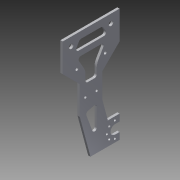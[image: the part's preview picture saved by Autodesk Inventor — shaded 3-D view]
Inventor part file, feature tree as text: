
AUTODESK INVENTOR PART (.ipt)
format: ipt  version: 2013 (Build 170138000, 138)  size: 265,728 bytes
history: native  units: mm
features: sketch x8, extrude x6, fillet x3, hole x2, other x1, pattern_circular x1
ambient origin geometry x8: Origin, YZ Plane, XZ Plane, XY Plane, X Axis, Y Axis, Z Axis, Center Point
feature tree (21):
  other  "ソリッド1"
  extrude  "押し出し1"  Depth=50.0mm
  extrude  "押し出し2"  Depth=100.0mm
  extrude  "押し出し5"  Depth=50.0mm
  hole  "穴1"  [1 undecoded]
  pattern_circular  "円形状パターン2"  [2 undecoded]
  hole  "穴2"  [1 undecoded]
  extrude  "押し出し7"  TaperAngle=135.0deg  [1 undecoded]
  extrude  "押し出し8"  Depth=25.0mm
  fillet  "フィレット1"  Radius=25.0mm
  fillet  "フィレット2"  Radius=50.0mm
  extrude  "押し出し9"  TaperAngle=165.0deg  [1 undecoded]
  fillet  "フィレット3"  Radius=20.0mm
  sketch  "スケッチ1"
  sketch  "スケッチ2"
  sketch  "スケッチ3"
  sketch  "スケッチ4"
  sketch  "スケッチ5"
  sketch  "スケッチ7"
  sketch  "スケッチ8"
  sketch  "スケッチ10"
note: 6 required parameter values undecoded (feature->parameter linkage not recoverable at this tier; creation-order binding heuristic only, values carry confidence <= 0.55)
